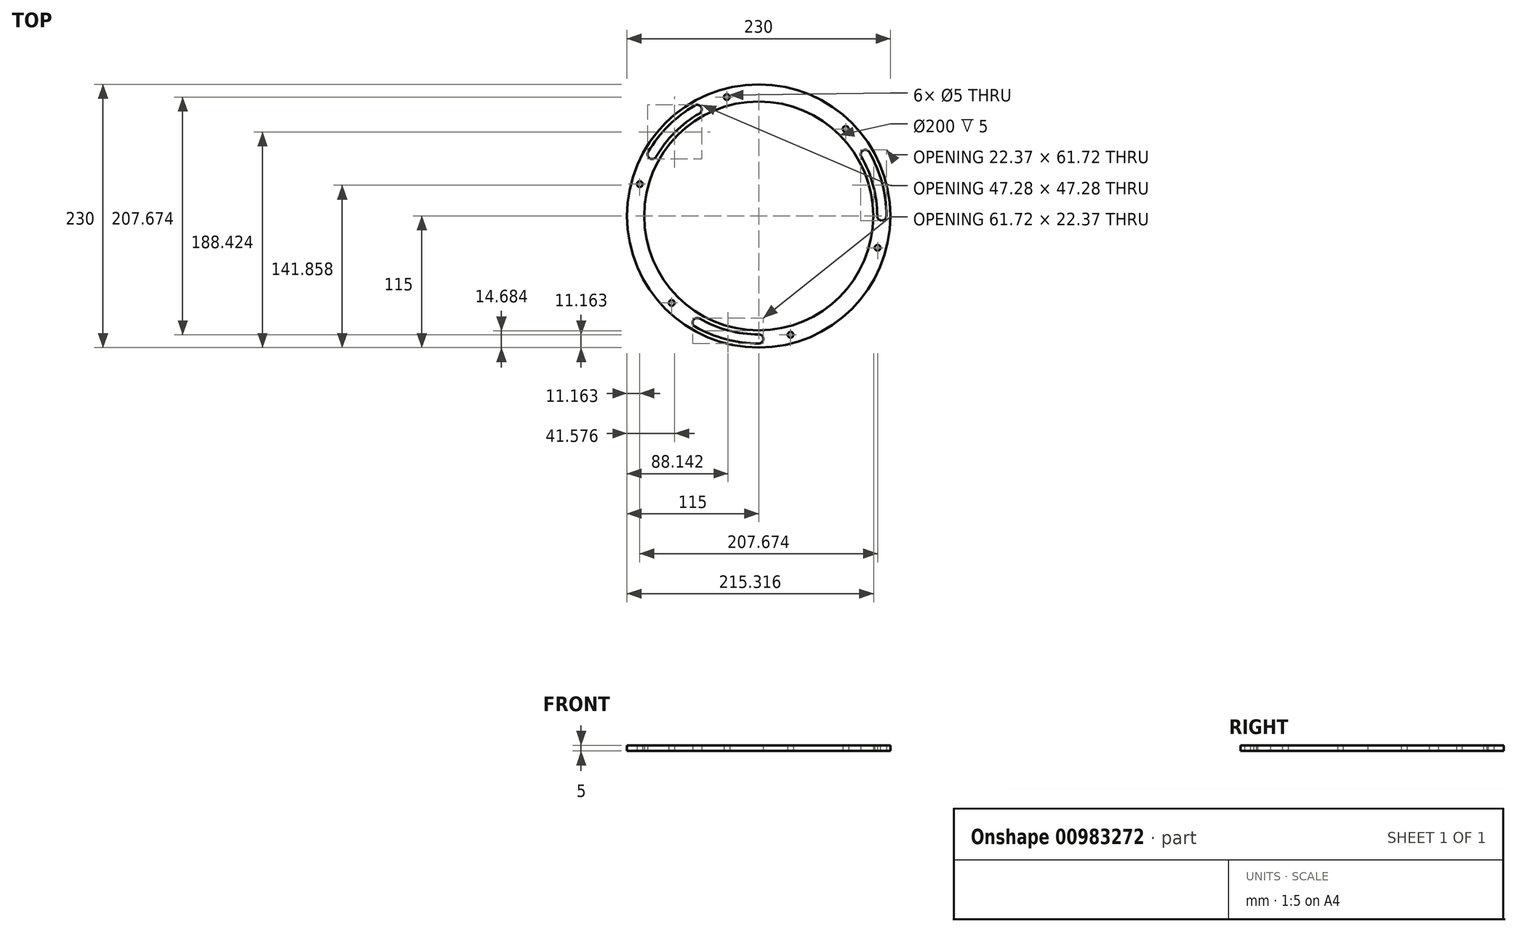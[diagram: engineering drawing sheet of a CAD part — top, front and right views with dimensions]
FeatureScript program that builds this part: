
annotation { "Feature Type Name" : "Feature", "Feature Type Description" : "" }
export const myFeature = defineFeature(function(context is Context, id is Id, definition is map)
    precondition{}
    {
        {
            var Q0;
            Q0=qCreatedBy(makeId("Top.planeOp"),FACE);
            var sketch = newSketch(context, id + "F0", { "sketchPlane" : qUnion([Q0])});
            skCircle(sketch, "E0", {"center": v(0, 0) * mm, "radius": 115 * mm});
            skCircle(sketch, "E1", {"center": v(0, 0) * mm, "radius": 120 * mm});
            skCircle(sketch, "E2", {"center": v(0, 0) * mm, "radius": 100 * mm});
            skPoint(sketch, "E3", {"position": v(100, 0) * mm});
            skPoint(sketch, "E4", {"position": v(107.5, 0) * mm});
            skPoint(sketch, "E5", {"position": v(115, 0) * mm});
            skCircle(sketch, "E6", {"center": v(0, 0) * mm, "radius": 60 * mm});
            skPoint(sketch, "E7", {"position": v(103.5, 0) * mm});
            skPoint(sketch, "E8", {"position": v(111.5, 0) * mm});
            skPoint(sketch, "E9.1.1", {"position": v(96.56, 55.75) * mm});
            skPoint(sketch, "E9.1.2", {"position": v(89.63, 51.75) * mm});
            skArc(sketch, "E10", {"start": v(103.5, 0) * mm, "mid": v(99.97, 26.79) * mm, "end": v(89.63, 51.75) * mm});
            skArc(sketch, "E11", {"start": v(111.5, 0) * mm, "mid": v(107.7, 28.86) * mm, "end": v(96.56, 55.75) * mm});
            skArc(sketch, "E12", {"start": v(89.63, 51.75) * mm, "mid": v(91.1, 57.21) * mm, "end": v(96.56, 55.75) * mm});
            skArc(sketch, "E13", {"start": v(103.5, 0) * mm, "mid": v(107.5, -4) * mm, "end": v(111.5, 0) * mm});
            skArc(sketch, "E14.1.0", {"start": v(-55.75, 96.56) * mm, "mid": v(-78.84, 78.84) * mm, "end": v(-96.56, 55.75) * mm});
            skArc(sketch, "E14.1.1", {"start": v(-51.75, 89.63) * mm, "mid": v(-73.19, 73.19) * mm, "end": v(-89.63, 51.75) * mm});
            skArc(sketch, "E14.1.2", {"start": v(-51.75, 89.63) * mm, "mid": v(-50.29, 95.1) * mm, "end": v(-55.75, 96.56) * mm});
            skArc(sketch, "E14.1.3", {"start": v(-89.63, 51.75) * mm, "mid": v(-95.1, 50.29) * mm, "end": v(-96.56, 55.75) * mm});
            skArc(sketch, "E14.2.0", {"start": v(-55.75, -96.56) * mm, "mid": v(-28.86, -107.7) * mm, "end": v(0, -111.5) * mm});
            skArc(sketch, "E14.2.1", {"start": v(-51.75, -89.63) * mm, "mid": v(-26.79, -99.97) * mm, "end": v(0, -103.5) * mm});
            skArc(sketch, "E14.2.2", {"start": v(-51.75, -89.63) * mm, "mid": v(-57.21, -91.1) * mm, "end": v(-55.75, -96.56) * mm});
            skArc(sketch, "E14.2.3", {"start": v(0, -103.5) * mm, "mid": v(4, -107.5) * mm, "end": v(0, -111.5) * mm});
            skPoint(sketch, "E15", {"position": v(103.84, -27.82) * mm});
            skCircle(sketch, "E16", {"center": v(103.84, -27.82) * mm, "radius": 2.5 * mm});
            skCircle(sketch, "E17.1.0", {"center": v(76.01, 76.01) * mm, "radius": 2.5 * mm});
            skCircle(sketch, "E17.2.0", {"center": v(-27.82, 103.84) * mm, "radius": 2.5 * mm});
            skCircle(sketch, "E17.3.0", {"center": v(-103.84, 27.82) * mm, "radius": 2.5 * mm});
            skCircle(sketch, "E17.4.0", {"center": v(-76.01, -76.01) * mm, "radius": 2.5 * mm});
            skCircle(sketch, "E17.5.0", {"center": v(27.82, -103.84) * mm, "radius": 2.5 * mm});
            skSolve(sketch);
        }
        {
            var Q0;
            Q0=makeQuery(id+"F0.imprint","IMPRINT",FACE,{"disambiguationData":[TD([[makeQuery(id+"F0.imprint","IMPRINT",EDGE,{"derivedFrom":sQuery(id+"F0.wireOp",EDGE,"E0")}),1.0]])]});
            extrude(context, id + "F1", {"entities" : qUnion([Q0]), "depth" : 5 * mm, "offsetDistance" : 25 * mm});
        }
    });
